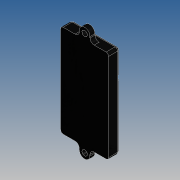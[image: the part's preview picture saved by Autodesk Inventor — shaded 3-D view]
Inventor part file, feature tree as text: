
AUTODESK INVENTOR PART (.ipt)
format: ipt  version: 2015 SP1 (Build 190203100, 203)  size: 577,024 bytes
history: native  units: mm
features: sketch x15, extrude x10, fillet x7, mirror x5, plane x4, sweep x2, chamfer x2, shell x1, hole x1, projected_geometry x1
ambient origin geometry x8: Origin, YZ Plane, XZ Plane, XY Plane, X Axis, Y Axis, Z Axis, Center Point
bodies: Solid1 (feature_tree)
feature tree (48):
  extrude  "Extrusion1"  Depth=29.0mm
  shell  "Shell1"  Thickness=112.0mm
  extrude  "Extrusion2"  Depth=2.0mm
  fillet  "Fillet1"  Radius=30.0mm
  fillet  "Fillet2"  Radius=130.0mm
  extrude  "Extrusion3"  Depth=1.0mm
  fillet  "Fillet3"  Radius=3.2mm
  extrude  "Extrusion4"  Depth=2.0mm
  fillet  "Fillet6"  Radius=2.0mm
  hole  "Hole1"  [1 undecoded]
  plane  "Work Plane1"
  fillet  "Fillet7"  Radius=3.0mm
  mirror  "Mirror3"
  mirror  "Mirror4"
  extrude  "Extrusion6"  Depth=6.5mm
  sweep  "Sweep1"
  sweep  "Sweep3"
  fillet  "Fillet8"  Radius=3.2mm
  mirror  "Mirror1"
  extrude  "Extrusion5"  Depth=12.0mm
  extrude  "Extrusion7"  Depth=6.0mm TaperAngle=0.0deg
  plane  "Work Plane2"
  extrude  "Extrusion8"  Depth=2.5mm
  extrude  "Extrusion9"  Depth=0.3mm
  extrude  "Extrusion10"  Depth=2.0mm
  chamfer  "Chamfer1"  Distance=2.0mm
  chamfer  "Chamfer2"  Distance=1.0mm
  fillet  "Fillet9"  Radius=1.0mm
  plane  "Work Plane3"
  mirror  "Mirror5"
  plane  "Work Plane4"
  mirror  "Mirror6"
  sketch  "Sketch1"  dims[d0=11.0mm d1=29.0mm d2=112.0mm d3=0.0mm]
  sketch  "Sketch2"  dims[d4=2.0mm d5=2.0mm d6=30.0mm d7=130.0mm d8=0.0mm]
  sketch  "Sketch3"  dims[d9=1.0mm d10=1.0mm d11=3.2mm]
  sketch  "Sketch4"  dims[d12=2.0mm d13=2.0mm d14=2.0mm]
  sketch  "Sketch5"  dims[d15=24.0mm d16=130.0mm d17=0.0mm d18=3.0mm]
  sketch  "Sketch6"  dims[d21=13.0mm d22=6.5mm]
  sketch  "Sketch7"  dims[d23=6.0mm d24=0.0mm d25=6.5mm]
  sketch  "Sketch8"  dims[d26=6.5mm d27=6.0mm d28=4.0mm d29=2.0mm d30=90.0deg d31=8.0mm d32=20.594885mm d33=5.0mm d34=3.2mm]
  sketch  "3D Sketch1"
  sketch  "Sketch10"  dims[d35=4.2mm d36=12.0mm]
  sketch  "Sketch11"  dims[d37=12.0mm d38=6.0mm d39=0.0mm]
  sketch  "3D Sketch3"
  sketch  "Sketch12"  dims[d40=2.0mm d42=2.0mm d43=0.0mm d44=2.5mm]
  sketch  "Sketch13"  dims[d45=0.8mm d46=0.3mm]
  sketch  "Sketch14"  dims[d47=0.0mm d48=0.0mm d53=2.0mm d55=2.0mm d56=0.0mm d57=1.0mm d58=1.0mm d59=0.3mm d60=0.8mm d61=0.0mm d62=0.0mm d63=0.4mm d64=2.0mm d65=3.5mm d66=3.5mm d69=2.0mm d70=0.0mm d71=1.5mm d72=1.5mm d73=1.8mm d74=0.0mm d75=0.4mm d76=0.4mm d77=2.0mm d78=0.0mm d79=2.0mm d80=2.0mm d81=15.0deg d82=2.0mm d83=2.0mm d84=15.0deg d85=0.4mm d86=19.9mm d87=15.5mm]
  projected_geometry  "Project Cut Edges1"
note: 1 required parameter value undecoded (feature->parameter linkage not recoverable at this tier; creation-order binding heuristic only, values carry confidence <= 0.55)
